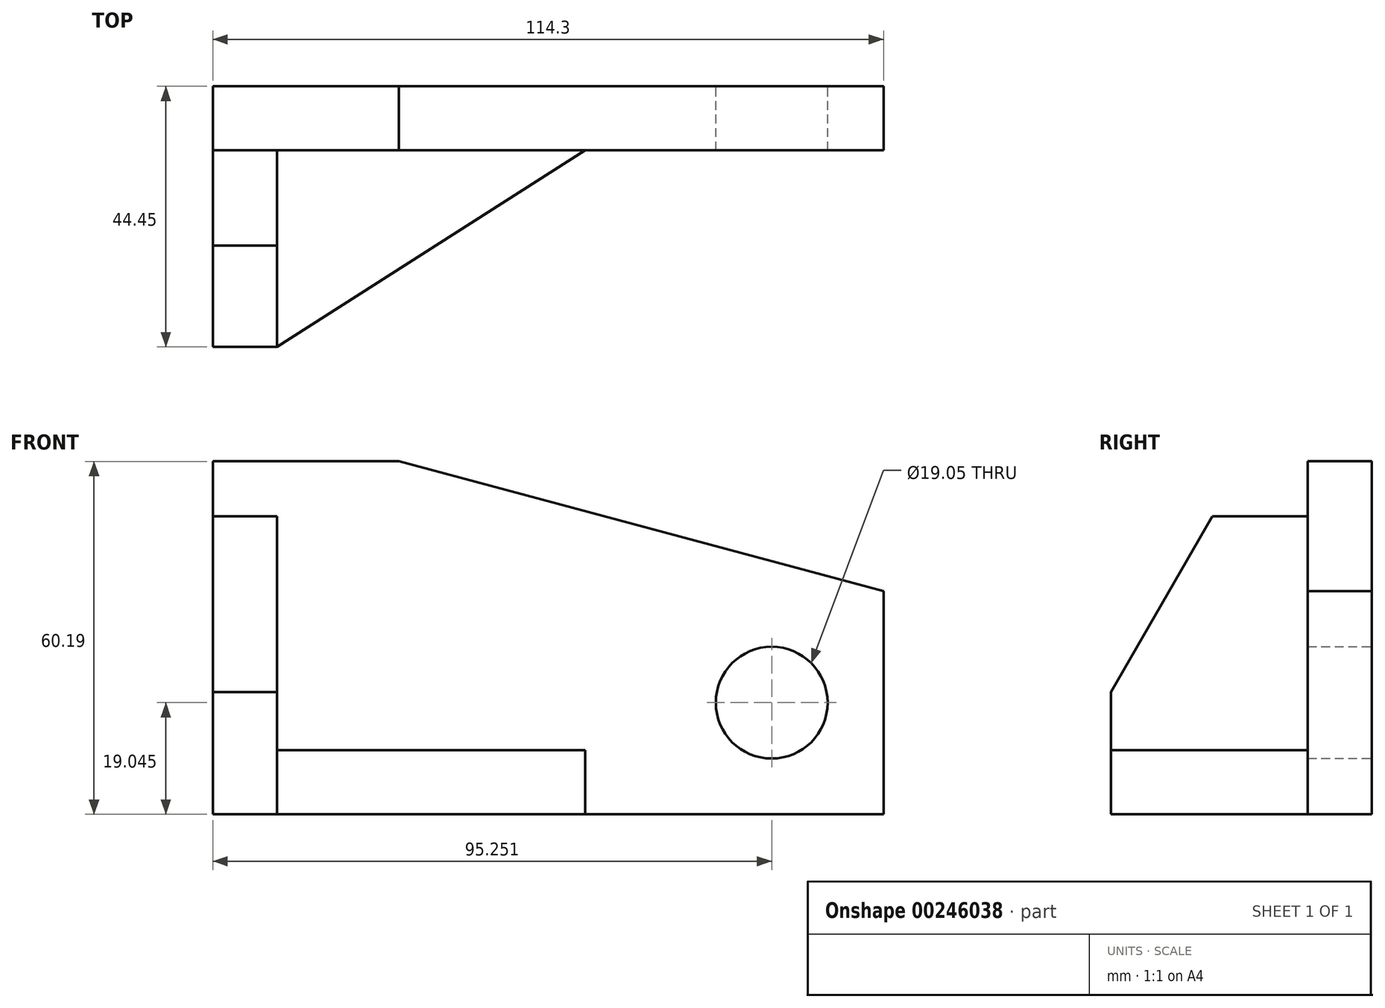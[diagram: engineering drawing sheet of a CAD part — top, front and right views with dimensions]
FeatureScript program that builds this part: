
annotation { "Feature Type Name" : "Feature", "Feature Type Description" : "" }
export const myFeature = defineFeature(function(context is Context, id is Id, definition is map)
    precondition{}
    {
        {
            var Q0;
            Q0=qCreatedBy(makeId("Front.planeOp"),FACE);
            var sketch = newSketch(context, id + "F0", { "sketchPlane" : qUnion([Q0])});
            skLineSegment(sketch, "E0.bottom", {"start": v(-58.96, 23.33) * mm, "end": v(-27.2, 23.33) * mm});
            skLineSegment(sketch, "E0.top", {"start": v(-58.96, -36.86) * mm, "end": v(55.34, -36.86) * mm});
            skLineSegment(sketch, "E0.left", {"start": v(-58.96, 23.33) * mm, "end": v(-58.96, -36.86) * mm});
            skLineSegment(sketch, "E0.right", {"start": v(55.34, 1.21) * mm, "end": v(55.34, -36.86) * mm});
            skLineSegment(sketch, "E1", {"start": v(-27.2, 23.33) * mm, "end": v(55.34, 1.21) * mm});
            skCircle(sketch, "E2", {"center": v(36.3, -17.81) * mm, "radius": 9.53 * mm});
            skLineSegment(sketch, "E3", {"start": v(36.3, -17.81) * mm, "end": v(36.3, -36.86) * mm, "construction": true});
            skLineSegment(sketch, "E4", {"start": v(36.3, -17.81) * mm, "end": v(55.34, -17.81) * mm, "construction": true});
            skSolve(sketch);
        }
        {
            var Q0;
            Q0 = qSketchRegion(id + "F0", true);
            extrude(context, id + "F1", {"entities" : qUnion([Q0]), "depth" : 10.92 * mm});
        }
        {
            var Q0;
            Q0=makeQuery(id+"F1.opExtrude","CAP_FACE",FACE,{"disambiguationData":[OSD([sQuery(id+"F0.wireOp",EDGE,"E0.bottom"),sQuery(id+"F0.wireOp",EDGE,"E0.top"),sQuery(id+"F0.wireOp",EDGE,"E0.left"),sQuery(id+"F0.wireOp",EDGE,"E0.right"),sQuery(id+"F0.wireOp",EDGE,"E1")])],"isStart":false});
            var sketch = newSketch(context, id + "F2", { "sketchPlane" : qUnion([Q0])});
            skLineSegment(sketch, "E5.bottom", {"start": v(-48.04, -25.94) * mm, "end": v(4.54, -25.94) * mm});
            skLineSegment(sketch, "E5.top", {"start": v(-48.04, -36.86) * mm, "end": v(4.54, -36.86) * mm});
            skLineSegment(sketch, "E5.left", {"start": v(-48.04, -25.94) * mm, "end": v(-48.04, -36.86) * mm});
            skLineSegment(sketch, "E5.right", {"start": v(4.54, -25.94) * mm, "end": v(4.54, -36.86) * mm});
            skLineSegment(sketch, "E6", {"start": v(-48.04, -25.94) * mm, "end": v(-58.96, -25.94) * mm, "construction": true});
            skSolve(sketch);
        }
        {
            var Q0;
            Q0=makeQuery(id+"F2.imprint","IMPRINT",FACE,{"disambiguationData":[TD([[makeQuery(id+"F2.imprint","IMPRINT",EDGE,{"derivedFrom":sQuery(id+"F2.wireOp",EDGE,"E5.bottom")}),-1.0]])]});
            extrude(context, id + "F3", {"entities" : qUnion([Q0]), "operationType" : NewBodyOperationType.ADD, "depth" : 33.53 * mm});
        }
        {
            var Q0;
            Q0=makeQuery(id+"F3.opExtrude","CAP_EDGE",EDGE,{"disambiguationData":[OSD([sQuery(id+"F2.wireOp",EDGE,"E5.right")])],"isStart":false});
            chamfer(context, id + "F4", {"entities" : qUnion([Q0]), "chamferType" : ChamferType.TWO_OFFSETS, "width1" : 33.53 * mm, "oppositeDirection" : false, "width2" : 52.58 * mm, "tangentPropagation" : true});
        }
        {
            var Q0;
            Q0=makeQuery(id+"F1.opExtrude","CAP_FACE",FACE,{"disambiguationData":[OSD([sQuery(id+"F0.wireOp",EDGE,"E0.bottom"),sQuery(id+"F0.wireOp",EDGE,"E0.top"),sQuery(id+"F0.wireOp",EDGE,"E0.left"),sQuery(id+"F0.wireOp",EDGE,"E0.right"),sQuery(id+"F0.wireOp",EDGE,"E1")])],"isStart":false});
            var sketch = newSketch(context, id + "F5", { "sketchPlane" : qUnion([Q0])});
            skLineSegment(sketch, "E7.bottom", {"start": v(-58.96, 13.94) * mm, "end": v(-48.04, 13.94) * mm});
            skLineSegment(sketch, "E7.top", {"start": v(-58.96, -36.86) * mm, "end": v(-48.04, -36.86) * mm});
            skLineSegment(sketch, "E7.left", {"start": v(-58.96, 13.94) * mm, "end": v(-58.96, -36.86) * mm});
            skLineSegment(sketch, "E7.right", {"start": v(-48.04, 13.94) * mm, "end": v(-48.04, -36.86) * mm});
            skSolve(sketch);
        }
        {
            var Q0;
            Q0 = qSketchRegion(id + "F5", true);
            extrude(context, id + "F6", {"entities" : qUnion([Q0]), "operationType" : NewBodyOperationType.ADD, "depth" : 33.53 * mm});
        }
        {
            var Q0;
            Q0=makeQuery(id+"F6.opExtrude","CAP_EDGE",EDGE,{"disambiguationData":[OSD([sQuery(id+"F5.wireOp",EDGE,"E7.bottom")])],"isStart":false});
            chamfer(context, id + "F7", {"entities" : qUnion([Q0]), "chamferType" : ChamferType.OFFSET_ANGLE, "width" : 17.27 * mm, "oppositeDirection" : false, "angle" : 60 * degree, "tangentPropagation" : true});
        }
    });
